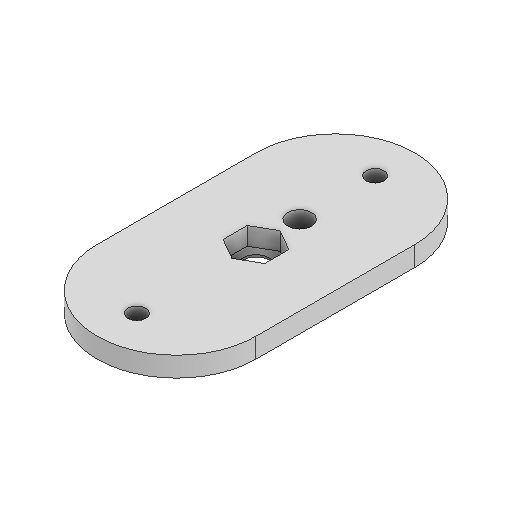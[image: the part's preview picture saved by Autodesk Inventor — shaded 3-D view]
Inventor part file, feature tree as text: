
AUTODESK INVENTOR PART (.ipt)
format: ipt  version: 2025.2 (Build 292293000, 293)  size: 125,440 bytes
history: native  units: mm
features: extrude x4, sketch x4
ambient origin geometry x8: Origin, YZ Plane, XZ Plane, XY Plane, X Axis, Y Axis, Z Axis, Center Point
bodies: Solid1 (feature_tree)
feature tree (8):
  extrude  "Extrusion1"  Depth=40.0mm
  extrude  "Extrusion2"  Depth=10.5mm
  extrude  "Extrusion3"  Depth=4.5mm
  extrude  "Extrusion4"  Depth=20.0mm
  sketch  "Sketch1"  dims[d0=40.0mm d1=80.0mm]
  sketch  "Sketch2"  dims[d2=5.0mm d3=0.0mm d4=10.5mm]
  sketch  "Sketch3"  dims[d5=4.5mm d6=0.0mm d7=6.5mm]
  sketch  "Sketch4"  dims[d8=0.0mm d9=0.0mm d10=6.0mm d11=11.0mm d12=4.5mm d13=4.5mm d14=30.0mm d15=30.0mm d16=0.0mm d17=0.0mm d18=20.0mm]
